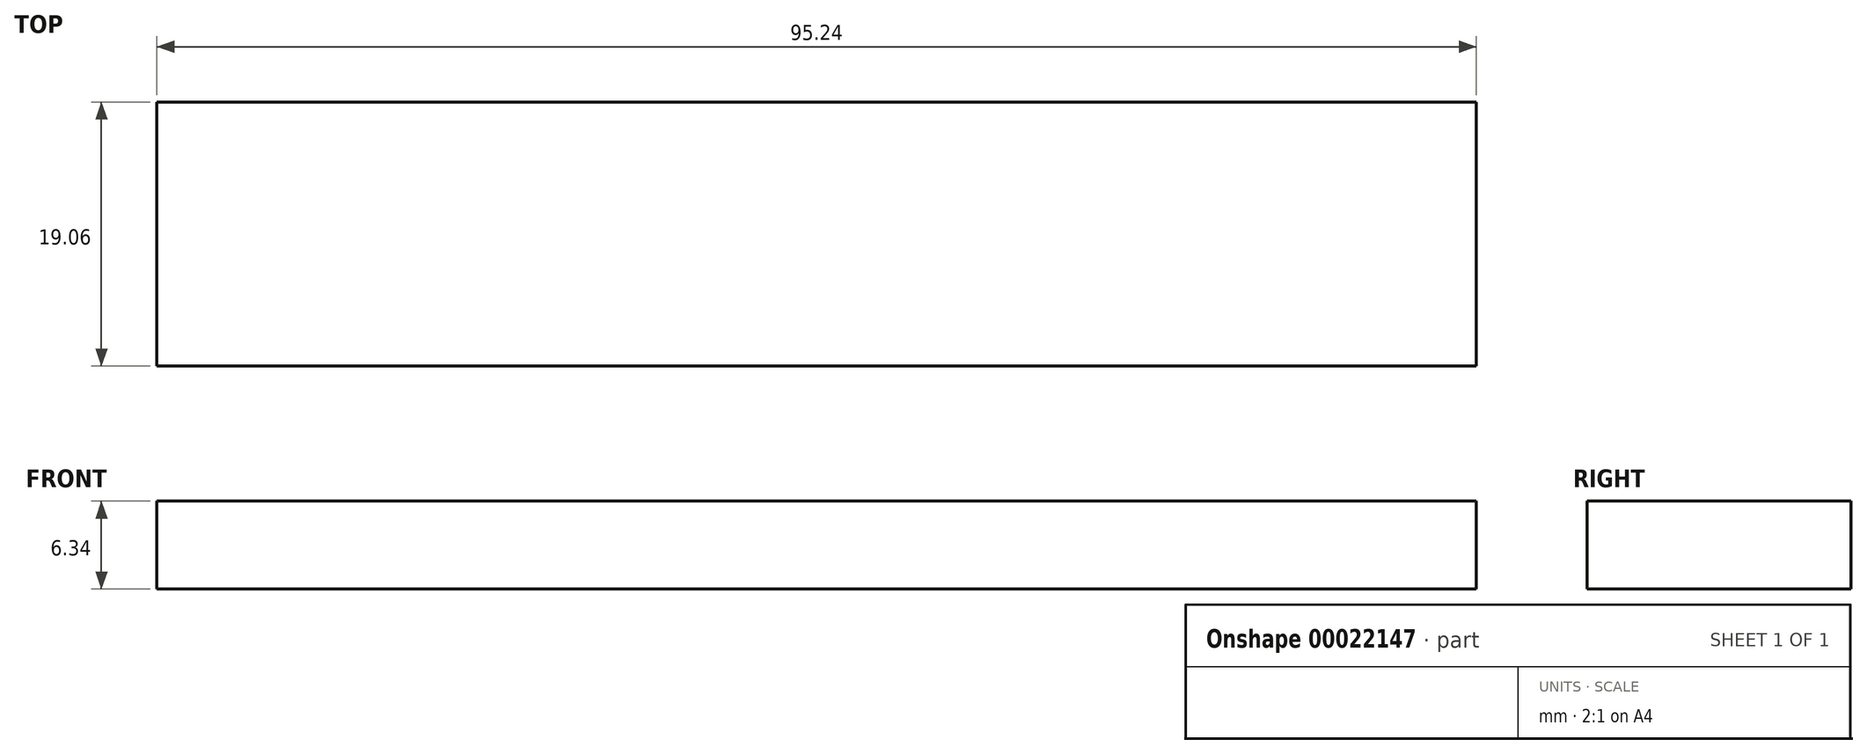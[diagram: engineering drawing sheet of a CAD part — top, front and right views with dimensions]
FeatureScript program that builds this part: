
annotation { "Feature Type Name" : "Feature", "Feature Type Description" : "" }
export const myFeature = defineFeature(function(context is Context, id is Id, definition is map)
    precondition{}
    {
        {
            var Q0;
            Q0=qCreatedBy(makeId("Right.planeOp"),FACE);
            var sketch = newSketch(context, id + "F0", { "sketchPlane" : qUnion([Q0])});
            skLineSegment(sketch, "E0.rect.bottom", {"start": v(9.53, 3.17) * mm, "end": v(-9.53, 3.17) * mm});
            skLineSegment(sketch, "E0.rect.top", {"start": v(9.53, -3.17) * mm, "end": v(-9.53, -3.17) * mm});
            skLineSegment(sketch, "E0.rect.left", {"start": v(9.53, 3.17) * mm, "end": v(9.53, -3.17) * mm});
            skLineSegment(sketch, "E0.rect.right", {"start": v(-9.53, 3.17) * mm, "end": v(-9.53, -3.17) * mm});
            skPoint(sketch, "E0.rect.middle", {"position": v(0, 0) * mm});
            skSolve(sketch);
        }
        {
            var Q0;
            Q0=makeQuery(id+"F0.imprint","IMPRINT",FACE,{"disambiguationData":[TD([[makeQuery(id+"F0.imprint","IMPRINT",EDGE,{"derivedFrom":sQuery(id+"F0.wireOp",EDGE,"E0.rect.bottom")}),1.0]])]});
            extrude(context, id + "F1", {"entities" : qUnion([Q0]), "endBound" : BoundingType.SYMMETRIC, "depth" : 95.25 * mm});
        }
    });
